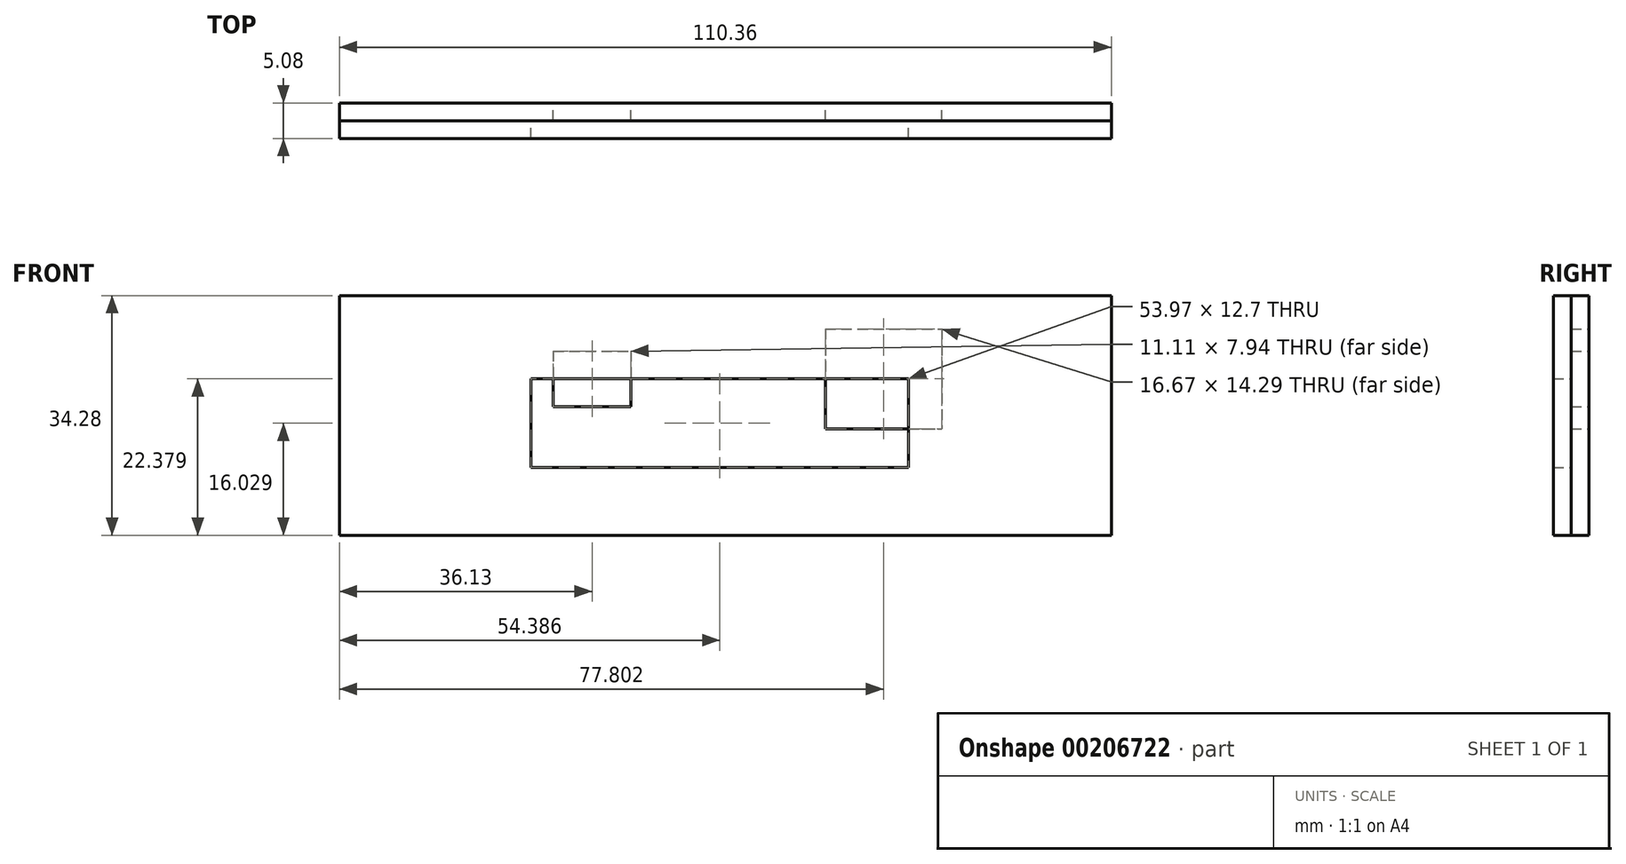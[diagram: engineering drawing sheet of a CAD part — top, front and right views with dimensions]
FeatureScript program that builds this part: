
annotation { "Feature Type Name" : "Feature", "Feature Type Description" : "" }
export const myFeature = defineFeature(function(context is Context, id is Id, definition is map)
    precondition{}
    {
        {
            var Q0;
            Q0=qCreatedBy(makeId("Front.planeOp"),FACE);
            var sketch = newSketch(context, id + "F0", { "sketchPlane" : qUnion([Q0])});
            skLineSegment(sketch, "E0.bottom", {"start": v(55.18, 17.15) * mm, "end": v(-55.18, 17.15) * mm});
            skLineSegment(sketch, "E0.top", {"start": v(55.18, -17.15) * mm, "end": v(-55.18, -17.15) * mm});
            skLineSegment(sketch, "E0.left", {"start": v(55.18, 17.15) * mm, "end": v(55.18, -17.15) * mm});
            skLineSegment(sketch, "E0.right", {"start": v(-55.18, 17.15) * mm, "end": v(-55.18, -17.15) * mm});
            skPoint(sketch, "E0.middle", {"position": v(0, 0) * mm});
            skLineSegment(sketch, "E1.bottom", {"start": v(-24.6, 9.2) * mm, "end": v(-13.5, 9.2) * mm});
            skLineSegment(sketch, "E1.top", {"start": v(-24.6, 1.27) * mm, "end": v(-13.5, 1.27) * mm});
            skLineSegment(sketch, "E1.left", {"start": v(-24.6, 9.2) * mm, "end": v(-24.6, 1.27) * mm});
            skLineSegment(sketch, "E1.right", {"start": v(-13.5, 9.2) * mm, "end": v(-13.5, 1.27) * mm});
            skLineSegment(sketch, "E2.bottom", {"start": v(14.29, 12.38) * mm, "end": v(30.96, 12.38) * mm});
            skLineSegment(sketch, "E2.top", {"start": v(14.29, -1.9) * mm, "end": v(30.96, -1.9) * mm});
            skLineSegment(sketch, "E2.left", {"start": v(14.29, 12.38) * mm, "end": v(14.29, -1.9) * mm});
            skLineSegment(sketch, "E2.right", {"start": v(30.96, 12.38) * mm, "end": v(30.96, -1.9) * mm});
            skSolve(sketch);
        }
        {
            var Q0;
            Q0 = qSketchRegion(id + "F0", true);
            extrude(context, id + "F1", {"entities" : qUnion([Q0]), "depth" : 2.54 * mm});
        }
        {
            var Q0;
            Q0=makeQuery(id+"F1.opExtrude","CAP_FACE",FACE,{"disambiguationData":[OSD([sQuery(id+"F0.wireOp",EDGE,"E0.bottom"),sQuery(id+"F0.wireOp",EDGE,"E0.top"),sQuery(id+"F0.wireOp",EDGE,"E0.left"),sQuery(id+"F0.wireOp",EDGE,"E0.right"),sQuery(id+"F0.wireOp",EDGE,"E1.bottom"),sQuery(id+"F0.wireOp",EDGE,"E1.top"),sQuery(id+"F0.wireOp",EDGE,"E1.left"),sQuery(id+"F0.wireOp",EDGE,"E1.right"),sQuery(id+"F0.wireOp",EDGE,"E2.bottom"),sQuery(id+"F0.wireOp",EDGE,"E2.top"),sQuery(id+"F0.wireOp",EDGE,"E2.left"),sQuery(id+"F0.wireOp",EDGE,"E2.right")])],"isStart":false});
            var sketch = newSketch(context, id + "F2", { "sketchPlane" : qUnion([Q0])});
            skLineSegment(sketch, "E3.bottom", {"start": v(-55.18, 17.15) * mm, "end": v(55.18, 17.15) * mm});
            skLineSegment(sketch, "E3.top", {"start": v(-55.18, -17.15) * mm, "end": v(55.18, -17.15) * mm});
            skLineSegment(sketch, "E3.left", {"start": v(-55.18, 17.15) * mm, "end": v(-55.18, -17.15) * mm});
            skLineSegment(sketch, "E3.right", {"start": v(55.18, 17.15) * mm, "end": v(55.18, -17.15) * mm});
            skLineSegment(sketch, "E4.bottom", {"start": v(-27.78, 5.24) * mm, "end": v(26.2, 5.24) * mm});
            skLineSegment(sketch, "E4.top", {"start": v(-27.78, -7.46) * mm, "end": v(26.2, -7.46) * mm});
            skLineSegment(sketch, "E4.left", {"start": v(-27.78, 5.24) * mm, "end": v(-27.78, -7.46) * mm});
            skLineSegment(sketch, "E4.right", {"start": v(26.2, 5.24) * mm, "end": v(26.2, -7.46) * mm});
            skSolve(sketch);
        }
        {
            var Q0;
            Q0 = qSketchRegion(id + "F2", true);
            extrude(context, id + "F3", {"entities" : qUnion([Q0]), "depth" : 2.54 * mm});
        }
    });
